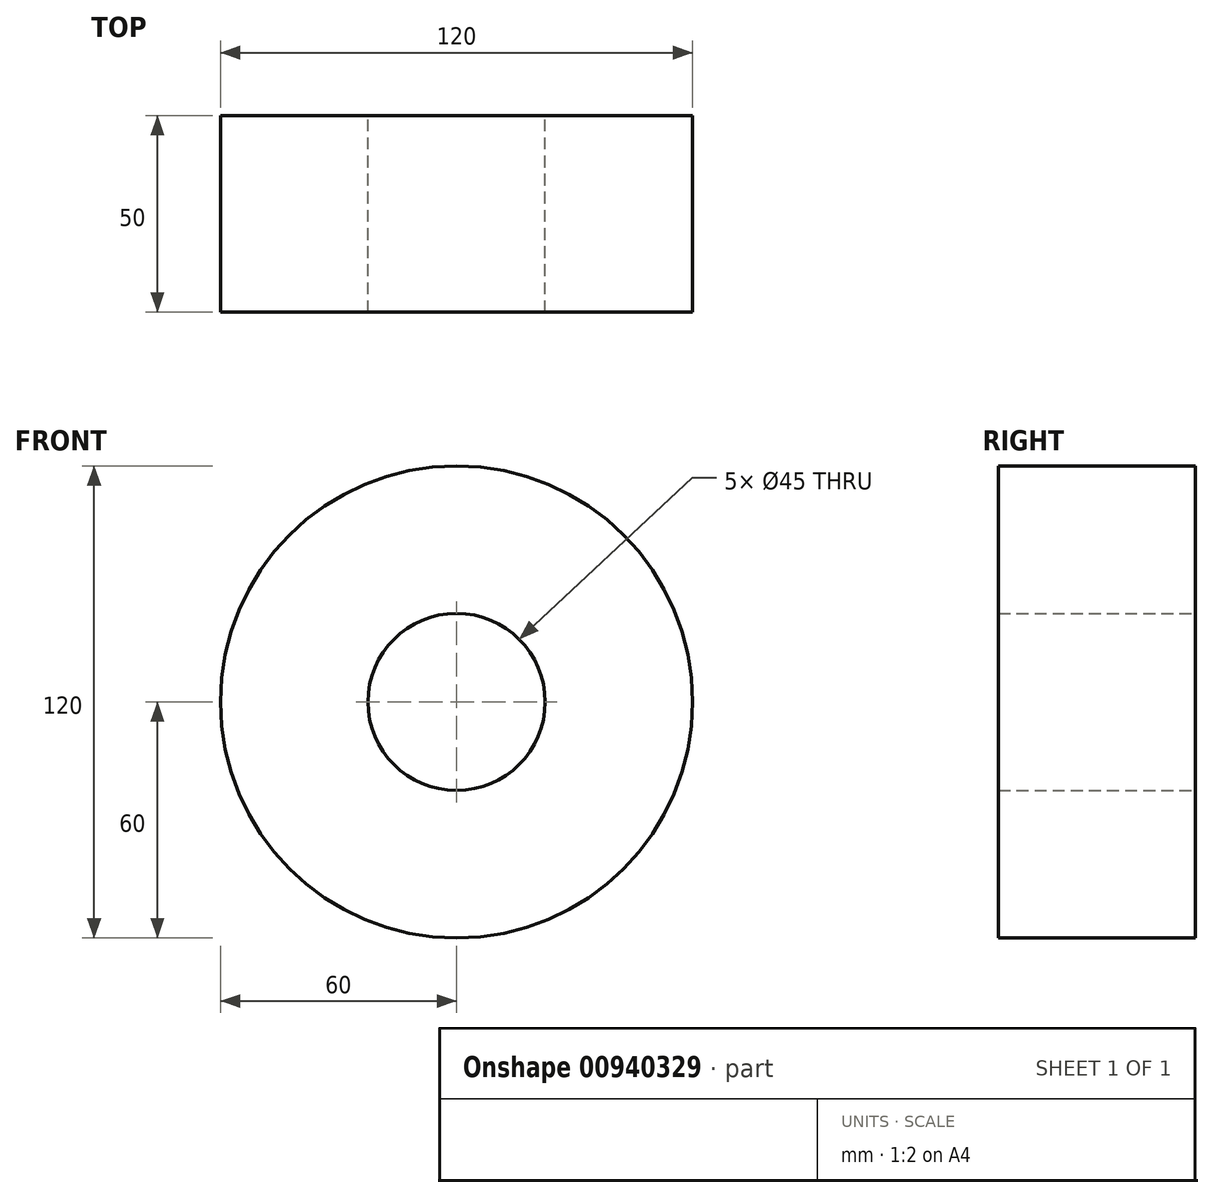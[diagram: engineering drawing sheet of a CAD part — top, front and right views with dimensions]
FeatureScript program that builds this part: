
annotation { "Feature Type Name" : "Feature", "Feature Type Description" : "" }
export const myFeature = defineFeature(function(context is Context, id is Id, definition is map)
    precondition{}
    {
        {
            var Q0;
            Q0=qCreatedBy(makeId("Front.planeOp"),FACE);
            var sketch = newSketch(context, id + "F0", { "sketchPlane" : qUnion([Q0])});
            skCircle(sketch, "E0", {"center": v(0, 0) * mm, "radius": 22.5 * mm});
            skCircle(sketch, "E1", {"center": v(0, 0) * mm, "radius": 60 * mm});
            skSolve(sketch);
        }
        {
            var Q0;
            Q0 = qSketchRegion(id + "F0", true);
            extrude(context, id + "F1", {"entities" : qUnion([Q0]), "depth" : 50 * mm, "offsetDistance" : 25 * mm});
        }
    });
